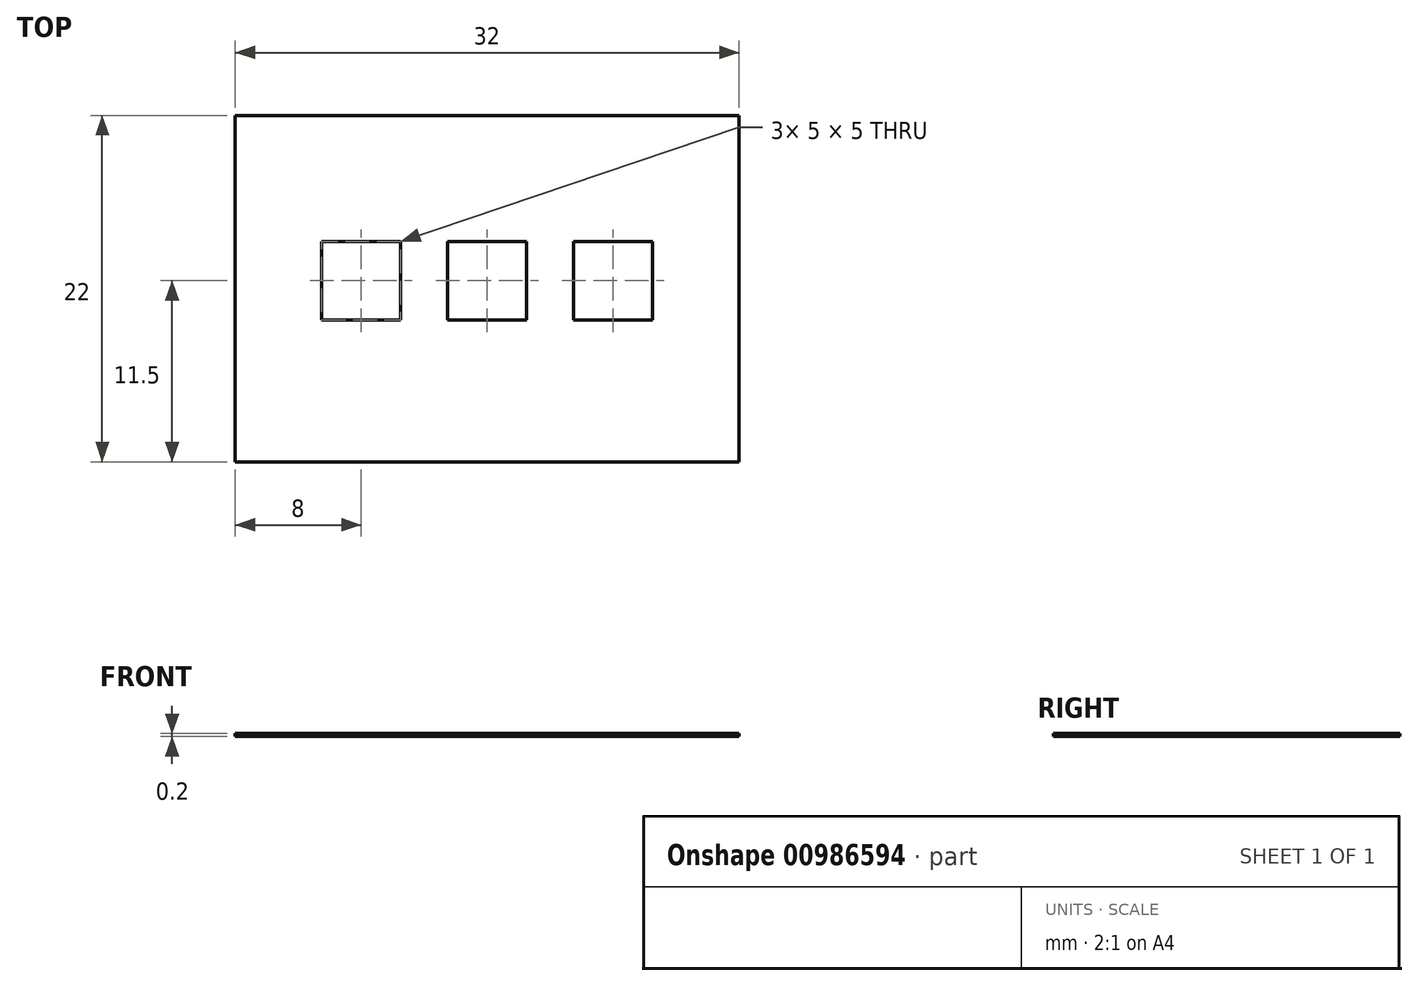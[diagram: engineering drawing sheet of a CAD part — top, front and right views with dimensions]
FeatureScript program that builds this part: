
annotation { "Feature Type Name" : "Feature", "Feature Type Description" : "" }
export const myFeature = defineFeature(function(context is Context, id is Id, definition is map)
    precondition{}
    {
        {
            var Q0;
            Q0=qCreatedBy(makeId("Top.planeOp"),FACE);
            var sketch = newSketch(context, id + "F0", { "sketchPlane" : qUnion([Q0])});
            skLineSegment(sketch, "E0.bottom", {"start": v(0, 0) * mm, "end": v(32, 0) * mm});
            skLineSegment(sketch, "E0.top", {"start": v(0, -22) * mm, "end": v(32, -22) * mm});
            skLineSegment(sketch, "E0.left", {"start": v(0, 0) * mm, "end": v(0, -22) * mm});
            skLineSegment(sketch, "E0.right", {"start": v(32, 0) * mm, "end": v(32, -22) * mm});
            skLineSegment(sketch, "E1.bottom", {"start": v(5.5, -8) * mm, "end": v(10.5, -8) * mm});
            skLineSegment(sketch, "E1.top", {"start": v(5.5, -13) * mm, "end": v(10.5, -13) * mm});
            skLineSegment(sketch, "E1.left", {"start": v(5.5, -8) * mm, "end": v(5.5, -13) * mm});
            skLineSegment(sketch, "E1.right", {"start": v(10.5, -8) * mm, "end": v(10.5, -13) * mm});
            skLineSegment(sketch, "E2.1.0.0", {"start": v(13.5, -8) * mm, "end": v(13.5, -13) * mm});
            skLineSegment(sketch, "E2.1.0.1", {"start": v(13.5, -8) * mm, "end": v(18.5, -8) * mm});
            skLineSegment(sketch, "E2.1.0.2", {"start": v(18.5, -8) * mm, "end": v(18.5, -13) * mm});
            skLineSegment(sketch, "E2.1.0.3", {"start": v(13.5, -13) * mm, "end": v(18.5, -13) * mm});
            skLineSegment(sketch, "E2.2.0.0", {"start": v(21.5, -8) * mm, "end": v(21.5, -13) * mm});
            skLineSegment(sketch, "E2.2.0.1", {"start": v(21.5, -8) * mm, "end": v(26.5, -8) * mm});
            skLineSegment(sketch, "E2.2.0.2", {"start": v(26.5, -8) * mm, "end": v(26.5, -13) * mm});
            skLineSegment(sketch, "E2.2.0.3", {"start": v(21.5, -13) * mm, "end": v(26.5, -13) * mm});
            skLineSegment(sketch, "E2.direction1", {"start": v(5.5, -13) * mm, "end": v(13.5, -13) * mm, "construction": true});
            skSolve(sketch);
        }
        {
            var Q0;
            Q0=makeQuery(id+"F0.imprint","IMPRINT",FACE,{"disambiguationData":[TD([[makeQuery(id+"F0.imprint","IMPRINT",EDGE,{"derivedFrom":sQuery(id+"F0.wireOp",EDGE,"E0.bottom")}),-1.0]])]});
            extrude(context, id + "F1", {"entities" : qUnion([Q0]), "depth" : 0.2 * mm, "offsetDistance" : 25.4 * mm});
        }
    });
